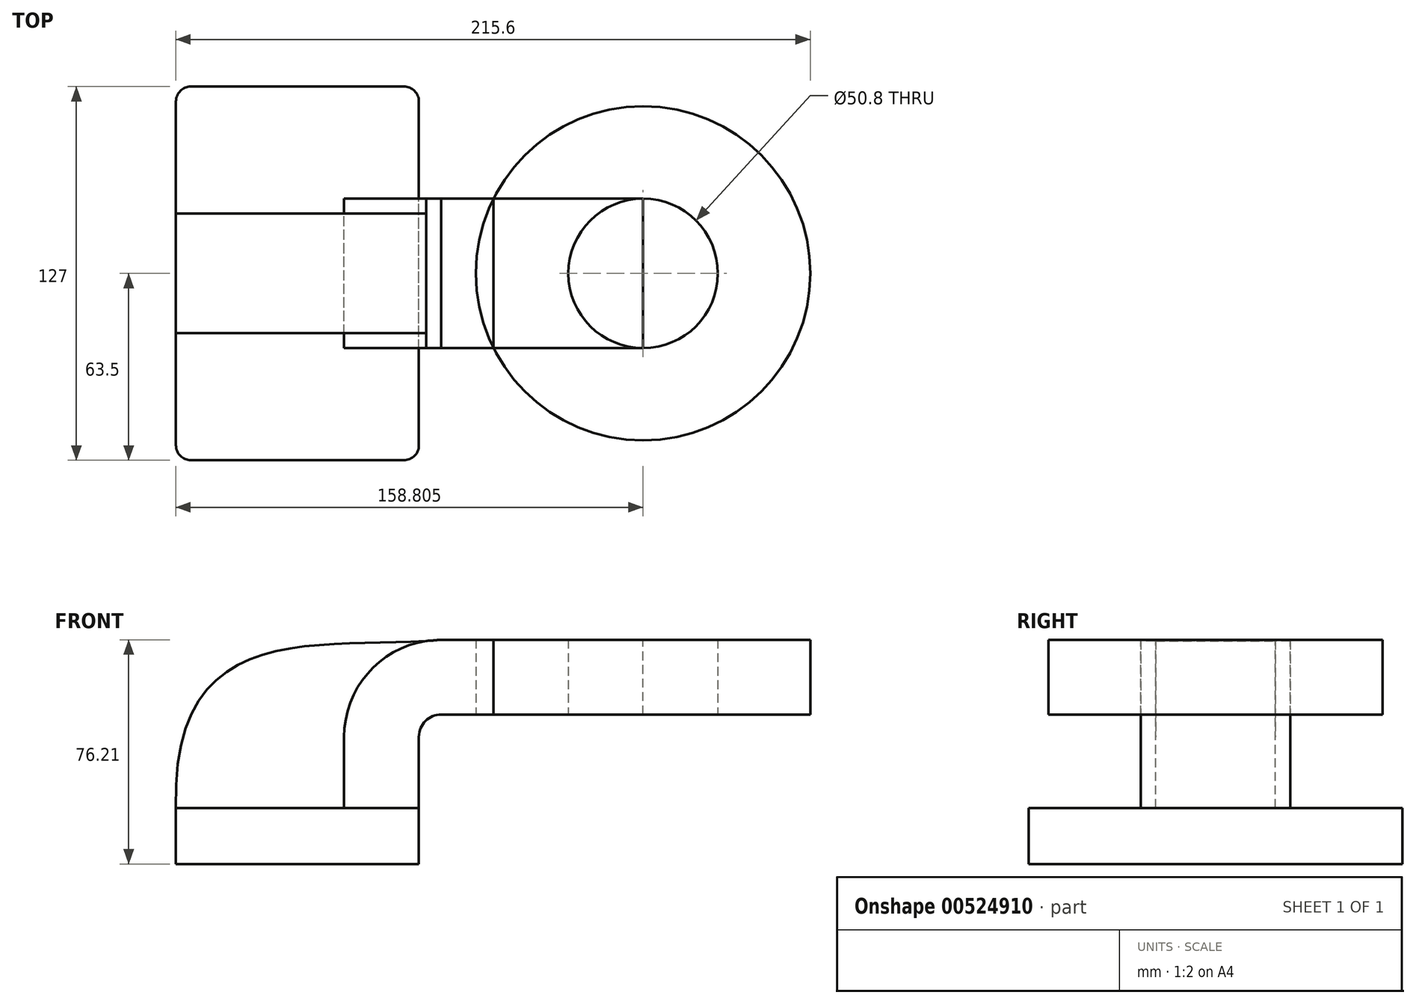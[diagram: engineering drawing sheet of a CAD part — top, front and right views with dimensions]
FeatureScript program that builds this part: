
annotation { "Feature Type Name" : "Feature", "Feature Type Description" : "" }
export const myFeature = defineFeature(function(context is Context, id is Id, definition is map)
    precondition{}
    {
        {
            var Q0;
            Q0=qCreatedBy(makeId("Front.planeOp"),FACE);
            var sketch = newSketch(context, id + "F0", { "sketchPlane" : qUnion([Q0])});
            skLineSegment(sketch, "E0.bottom", {"start": v(41.28, -9.52) * mm, "end": v(-41.28, -9.53) * mm});
            skLineSegment(sketch, "E0.top", {"start": v(41.28, 9.53) * mm, "end": v(-41.28, 9.53) * mm});
            skLineSegment(sketch, "E0.left", {"start": v(41.28, -9.52) * mm, "end": v(41.28, 9.53) * mm});
            skLineSegment(sketch, "E0.right", {"start": v(-41.28, -9.53) * mm, "end": v(-41.28, 9.53) * mm});
            skPoint(sketch, "E0.middle", {"position": v(0, 0) * mm});
            skLineSegment(sketch, "E1.bottom", {"start": v(117.48, 41.28) * mm, "end": v(66.67, 41.28) * mm});
            skLineSegment(sketch, "E1.top", {"start": v(117.48, 66.68) * mm, "end": v(66.68, 66.68) * mm});
            skLineSegment(sketch, "E1.left", {"start": v(117.48, 41.28) * mm, "end": v(117.48, 66.68) * mm});
            skLineSegment(sketch, "E1.right", {"start": v(66.67, 41.28) * mm, "end": v(66.67, 66.68) * mm});
            skPoint(sketch, "E1.middle", {"position": v(92.08, 53.98) * mm});
            skLineSegment(sketch, "E2", {"start": v(41.28, 9.53) * mm, "end": v(41.28, 33.66) * mm});
            skArc(sketch, "E3", {"start": v(41.27, 33.66) * mm, "mid": v(43.5, 39.04) * mm, "end": v(48.9, 41.28) * mm});
            skLineSegment(sketch, "E4", {"start": v(48.9, 41.28) * mm, "end": v(74.26, 41.28) * mm});
            skLineSegment(sketch, "E5.0", {"start": v(48.9, 66.68) * mm, "end": v(74.26, 66.68) * mm});
            skArc(sketch, "E5.1", {"start": v(15.88, 33.66) * mm, "mid": v(25.55, 57) * mm, "end": v(48.9, 66.68) * mm});
            skLineSegment(sketch, "E5.2", {"start": v(15.87, 9.53) * mm, "end": v(15.87, 33.66) * mm});
            skFitSpline(sketch, "E6", {"points": [v(-41.28, 9.53) * mm, v(48.9, 66.68) * mm], "startDerivative": vector(-5.89, 199.2) * mm, "endDerivative": vector(118.53, 11.47) * mm});
            skSolve(sketch);
        }
        {
            var Q0;
            Q0=makeQuery(id+"F0.imprint","IMPRINT",FACE,{"disambiguationData":[TD([[makeQuery(id+"F0.imprint","IMPRINT",EDGE,{"derivedFrom":sQuery(id+"F0.wireOp",EDGE,"E0.bottom")}),-1.0]])]});
            extrude(context, id + "F1", {"entities" : qUnion([Q0]), "endBound" : BoundingType.SYMMETRIC, "depth" : 127 * mm, "offsetDistance" : 25.4 * mm});
        }
        {
            var Q0;
            {var subQ3=sQuery(id+"F0.wireOp",EDGE,"E5.2");Q0=makeQuery(id+"F0.imprint","IMPRINT",FACE,{"disambiguationData":[TD([[makeQuery(id+"F0.imprint","IMPRINT",EDGE,{"derivedFrom":subQ3}),1.0]])]});}
            extrude(context, id + "F2", {"entities" : qUnion([Q0]), "operationType" : NewBodyOperationType.ADD, "endBound" : BoundingType.SYMMETRIC, "depth" : 40.64 * mm, "offsetDistance" : 25.4 * mm});
        }
        {
            var Q0;
            {var subQ2=sQuery(id+"F0.wireOp",EDGE,"E1.bottom");Q0=makeQuery(id+"F0.imprint","IMPRINT",FACE,{"disambiguationData":[TD([[makeQuery(id+"F0.imprint","IMPRINT",EDGE,{"derivedFrom":subQ2}),-1.0]])]});}
            extrude(context, id + "F3", {"entities" : qUnion([Q0]), "operationType" : NewBodyOperationType.ADD, "endBound" : BoundingType.SYMMETRIC, "depth" : 50.8 * mm, "offsetDistance" : 25.4 * mm});
        }
        {
            var Q0;
            {var subQ2=sQuery(id+"F0.wireOp",EDGE,"E1.right");Q0=makeQuery(id+"F0.imprint","IMPRINT",FACE,{"disambiguationData":[TD([[makeQuery(id+"F0.imprint","IMPRINT",EDGE,{"derivedFrom":subQ2}),1.0]])]});}
            extrude(context, id + "F4", {"entities" : qUnion([Q0]), "endBound" : BoundingType.SYMMETRIC, "depth" : 50.8 * mm, "offsetDistance" : 25.4 * mm});
        }
        {
            var Q0;
            Q0=makeQuery(id+"F1.opExtrude","CAP_EDGE",EDGE,{"disambiguationData":[OSD([sQuery(id+"F0.wireOp",EDGE,"E0.right")])],"isStart":false});
            var Q1;
            Q1=makeQuery(id+"F1.opExtrude","CAP_EDGE",EDGE,{"disambiguationData":[OSD([sQuery(id+"F0.wireOp",EDGE,"E0.left")])],"isStart":false});
            var Q2;
            Q2=makeQuery(id+"F1.opExtrude","CAP_EDGE",EDGE,{"disambiguationData":[OSD([sQuery(id+"F0.wireOp",EDGE,"E0.left")])],"isStart":true});
            var Q3;
            Q3=makeQuery(id+"F1.opExtrude","CAP_EDGE",EDGE,{"disambiguationData":[OSD([sQuery(id+"F0.wireOp",EDGE,"E0.right")])],"isStart":true});
            fillet(context, id + "F5", {"entities" : qUnion([Q0, Q1, Q2, Q3]), "radius" : 5.08 * mm, "tangentPropagation" : true, "allowEdgeOverflow" : false});
        }
        {
            var Q0;
            Q0=makeQuery(id+"F3.opExtrude","CAP_FACE",FACE,{"disambiguationData":[OSD([sQuery(id+"F0.wireOp",EDGE,"E1.bottom"),sQuery(id+"F0.wireOp",EDGE,"E1.top"),sQuery(id+"F0.wireOp",EDGE,"E1.left"),sQuery(id+"F0.wireOp",EDGE,"E1.right"),sQuery(id+"F0.wireOp",EDGE,"E4"),sQuery(id+"F0.wireOp",EDGE,"E5.0")])],"isStart":false});
            var Q1;
            Q1=sQuery(id+"F0.wireOp",EDGE,"E1.left");
            revolve(context, id + "F6", {"entities" : qUnion([Q0]), "axis" : qUnion([Q1]), "revolveType" : RevolveType.FULL});
        }
    });
